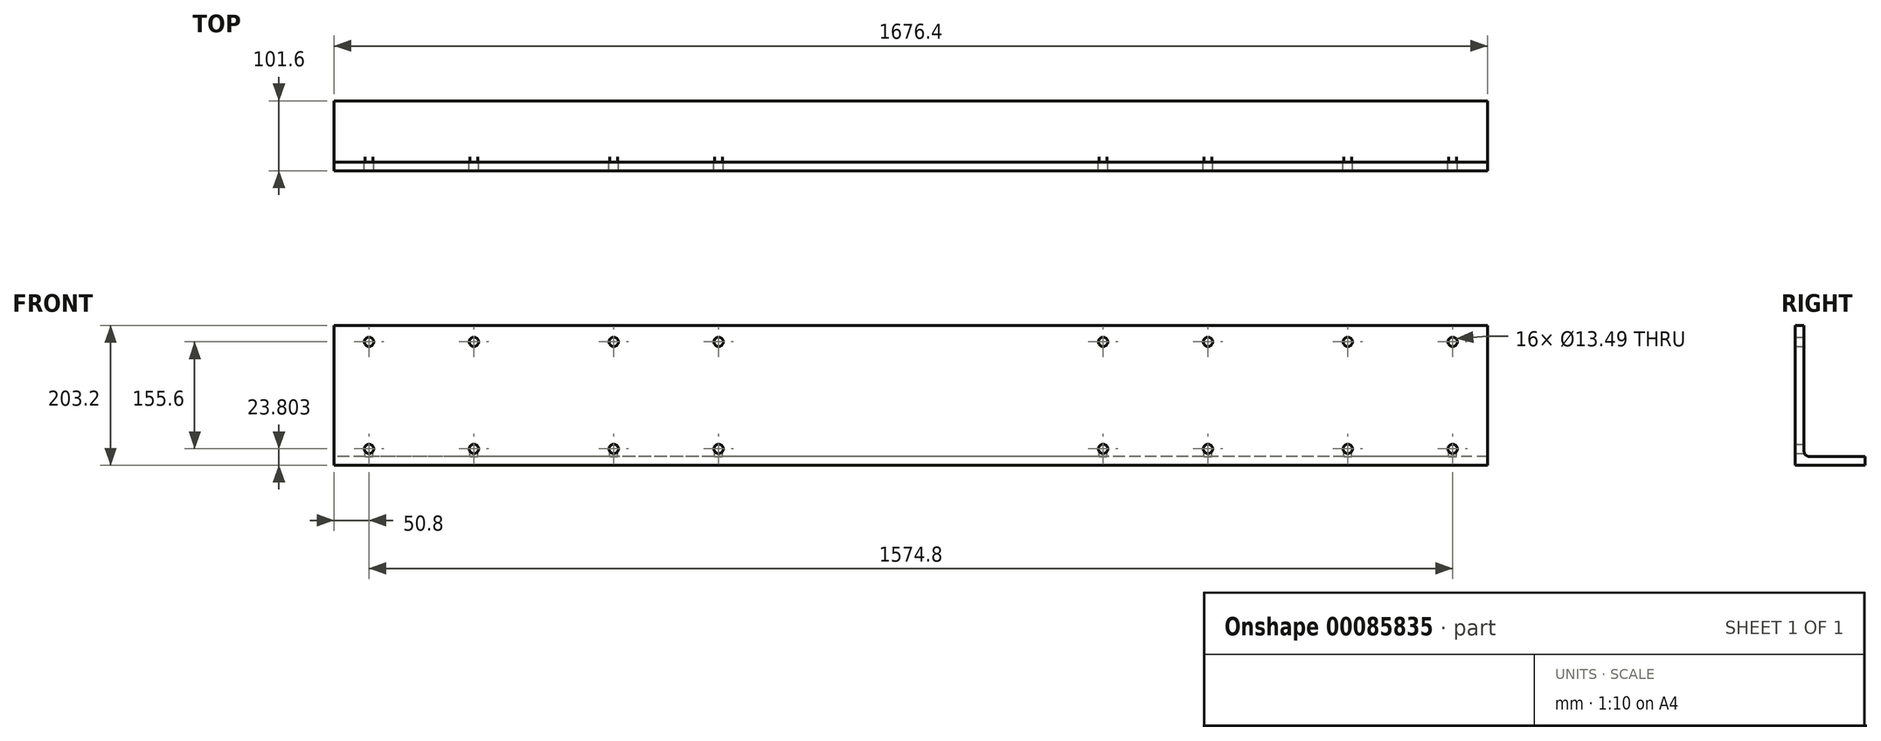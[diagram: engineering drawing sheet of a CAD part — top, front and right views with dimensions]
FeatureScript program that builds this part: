
annotation { "Feature Type Name" : "Feature", "Feature Type Description" : "" }
export const myFeature = defineFeature(function(context is Context, id is Id, definition is map)
    precondition{}
    {
        {
            var Q0;
            Q0=qCreatedBy(makeId("Right.planeOp"),FACE);
            var sketch = newSketch(context, id + "F0", { "sketchPlane" : qUnion([Q0])});
            skLineSegment(sketch, "E0", {"start": v(-89.64, 109.56) * mm, "end": v(-89.64, -93.64) * mm});
            skLineSegment(sketch, "E1", {"start": v(-89.64, -93.64) * mm, "end": v(11.96, -93.64) * mm});
            skLineSegment(sketch, "E2.0", {"start": v(-76.94, -80.94) * mm, "end": v(11.96, -80.94) * mm});
            skLineSegment(sketch, "E2.1", {"start": v(-76.94, 109.56) * mm, "end": v(-76.94, -80.94) * mm});
            skLineSegment(sketch, "E3", {"start": v(-89.64, 109.56) * mm, "end": v(-76.94, 109.56) * mm});
            skLineSegment(sketch, "E4", {"start": v(11.96, -80.94) * mm, "end": v(11.96, -93.64) * mm});
            skSolve(sketch);
        }
        {
            var Q0;
            Q0=makeQuery(id+"F0.imprint","IMPRINT",FACE,{"disambiguationData":[TD([[makeQuery(id+"F0.imprint","IMPRINT",EDGE,{"derivedFrom":sQuery(id+"F0.wireOp",EDGE,"E0")}),1.0]])]});
            extrude(context, id + "F1", {"entities" : qUnion([Q0]), "depth" : 1676.4 * mm, "offsetDistance" : 25.4 * mm});
        }
        {
            var Q0;
            Q0=makeQuery(id+"F1.opExtrude","SWEPT_FACE",FACE,{"disambiguationData":[OSD([sQuery(id+"F0.wireOp",EDGE,"E0")])]});
            var sketch = newSketch(context, id + "F2", { "sketchPlane" : qUnion([Q0])});
            skLineSegment(sketch, "E5", {"start": v(1676.4, 85.76) * mm, "end": v(1066.8, 85.76) * mm});
            skLineSegment(sketch, "E6", {"start": v(1676.4, -69.84) * mm, "end": v(1066.8, -69.84) * mm});
            skLineSegment(sketch, "E7", {"start": v(1625.6, 109.56) * mm, "end": v(1625.6, -93.64) * mm});
            skLineSegment(sketch, "E8", {"start": v(1473.2, 109.56) * mm, "end": v(1473.2, -93.64) * mm});
            skLineSegment(sketch, "E9", {"start": v(1371.6, 85.76) * mm, "end": v(1371.6, -69.84) * mm});
            skPoint(sketch, "E10", {"position": v(1473.2, 85.76) * mm});
            skPoint(sketch, "E11", {"position": v(1625.6, 85.76) * mm});
            skPoint(sketch, "E12", {"position": v(1625.6, -69.84) * mm});
            skPoint(sketch, "E13", {"position": v(1473.2, -69.84) * mm});
            skPoint(sketch, "E14.MirrorP", {"position": v(1270, 85.76) * mm});
            skPoint(sketch, "E15.MirrorP", {"position": v(1117.6, 85.76) * mm});
            skPoint(sketch, "E16.MirrorP", {"position": v(1117.6, -69.84) * mm});
            skPoint(sketch, "E17.MirrorP", {"position": v(1270, -69.84) * mm});
            skLineSegment(sketch, "E18", {"start": v(838.2, 109.56) * mm, "end": v(838.2, -93.64) * mm});
            skPoint(sketch, "E19.MirrorP", {"position": v(558.8, 85.76) * mm});
            skPoint(sketch, "E20.MirrorP", {"position": v(406.4, 85.76) * mm});
            skPoint(sketch, "E21.MirrorP", {"position": v(203.2, 85.76) * mm});
            skPoint(sketch, "E22.MirrorP", {"position": v(50.8, 85.76) * mm});
            skPoint(sketch, "E23.MirrorP", {"position": v(50.8, -69.84) * mm});
            skPoint(sketch, "E24.MirrorP", {"position": v(203.2, -69.84) * mm});
            skPoint(sketch, "E25.MirrorP", {"position": v(406.4, -69.84) * mm});
            skPoint(sketch, "E26.MirrorP", {"position": v(558.8, -69.84) * mm});
            skSolve(sketch);
        }
        {
            var Q0;
            Q0=sQuery(id+"F2.wireOp",VERTEX,"E10");
            var Q1;
            Q1=sQuery(id+"F2.wireOp",VERTEX,"E11");
            var Q2;
            Q2=sQuery(id+"F2.wireOp",VERTEX,"E12");
            var Q3;
            Q3=sQuery(id+"F2.wireOp",VERTEX,"E13");
            var Q4;
            Q4=sQuery(id+"F2.wireOp",VERTEX,"E17.MirrorP");
            var Q5;
            Q5=sQuery(id+"F2.wireOp",VERTEX,"E14.MirrorP");
            var Q6;
            Q6=sQuery(id+"F2.wireOp",VERTEX,"E15.MirrorP");
            var Q7;
            Q7=sQuery(id+"F2.wireOp",VERTEX,"E16.MirrorP");
            var Q8;
            Q8=sQuery(id+"F2.wireOp",VERTEX,"E19.MirrorP");
            var Q9;
            Q9=sQuery(id+"F2.wireOp",VERTEX,"E20.MirrorP");
            var Q10;
            Q10=sQuery(id+"F2.wireOp",VERTEX,"E21.MirrorP");
            var Q11;
            Q11=sQuery(id+"F2.wireOp",VERTEX,"E22.MirrorP");
            var Q12;
            Q12=sQuery(id+"F2.wireOp",VERTEX,"E23.MirrorP");
            var Q13;
            Q13=sQuery(id+"F2.wireOp",VERTEX,"E24.MirrorP");
            var Q14;
            Q14=sQuery(id+"F2.wireOp",VERTEX,"E25.MirrorP");
            var Q15;
            Q15=sQuery(id+"F2.wireOp",VERTEX,"E26.MirrorP");
            var Q16;
            Q16=makeQuery(id+"F1.opExtrude","SWEPT_BODY",BODY,{"disambiguationData":[OSD([sQuery(id+"F0.wireOp",EDGE,"E0"),sQuery(id+"F0.wireOp",EDGE,"E1"),sQuery(id+"F0.wireOp",EDGE,"E2.0"),sQuery(id+"F0.wireOp",EDGE,"E2.1"),sQuery(id+"F0.wireOp",EDGE,"E3"),sQuery(id+"F0.wireOp",EDGE,"E4")])]});
            hole(context, id + "F3", {"style" : HoleStyle.SIMPLE, "endStyle" : HoleEndStyle.THROUGH, "holeDiameter" : 13.5 * mm, "majorDiameter" : 6.35 * mm, "isTappedThrough" : true, "tappedDepth" : 19.05 * mm, "tapClearance" : 3, "startFromSketch" : true, "locations" : qUnion([Q0, Q1, Q2, Q3, Q4, Q5, Q6, Q7, Q8, Q9, Q10, Q11, Q12, Q13, Q14, Q15]), "scope" : qUnion([Q16])});
        }
        {
            var Q0;
            Q0=makeQuery(id+"F1.opExtrude","SWEPT_EDGE",EDGE,{"disambiguationData":[OSD([sQuery(id+"F0.wireOp",EDGE,"E2.0"),sQuery(id+"F0.wireOp",EDGE,"E2.1")])]});
            fillet(context, id + "F4", {"entities" : qUnion([Q0]), "radius" : 7.62 * mm, "tangentPropagation" : true, "allowEdgeOverflow" : false});
        }
    });
